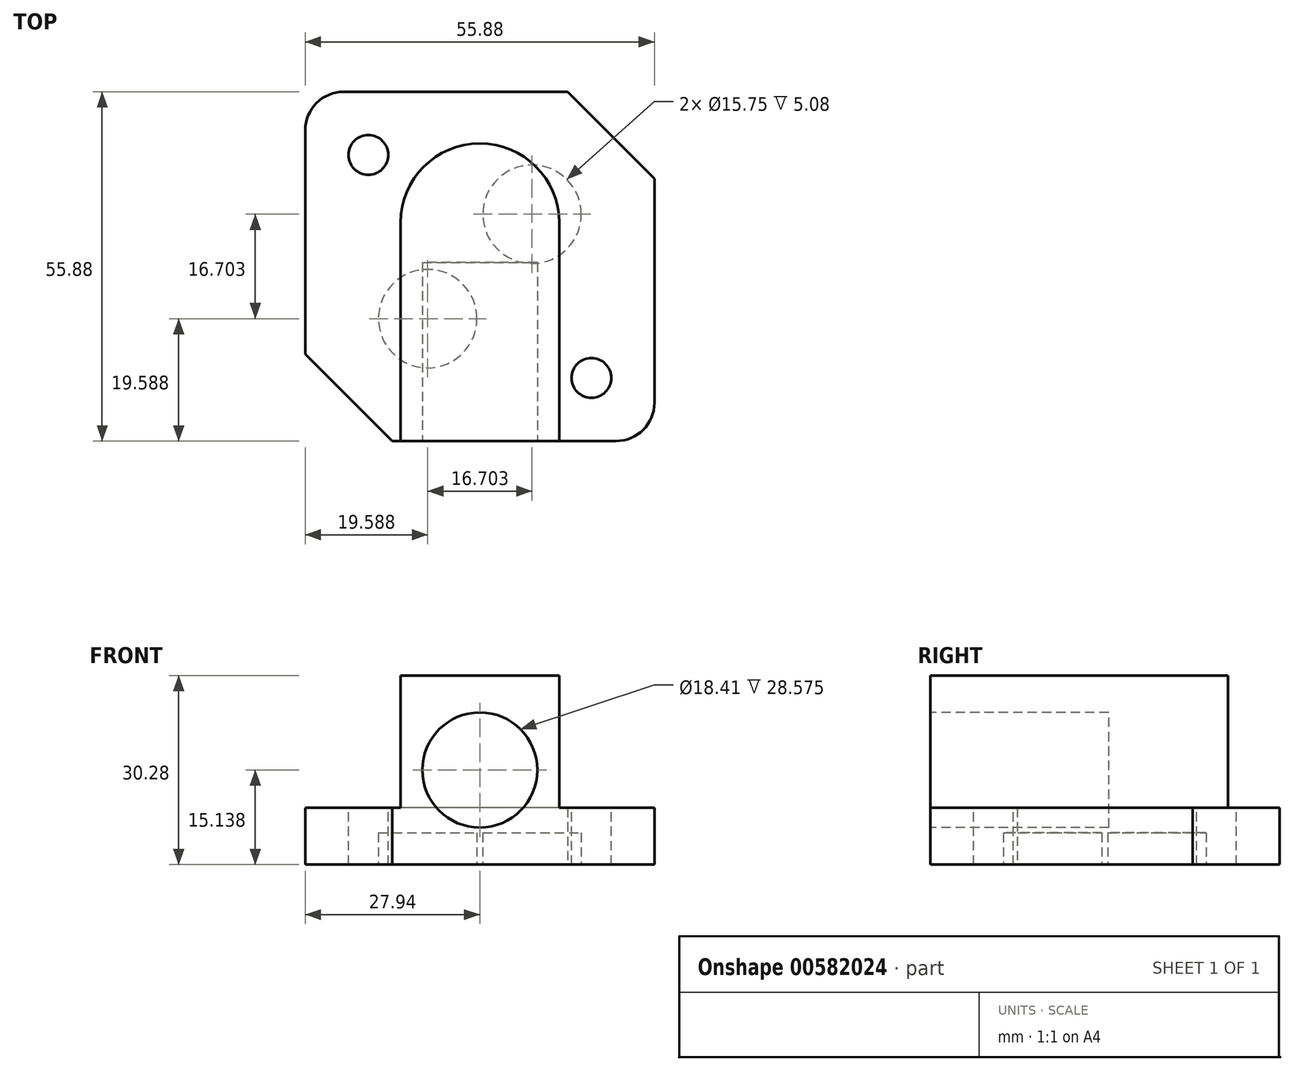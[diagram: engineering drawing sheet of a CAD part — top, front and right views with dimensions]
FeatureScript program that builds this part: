
annotation { "Feature Type Name" : "Feature", "Feature Type Description" : "" }
export const myFeature = defineFeature(function(context is Context, id is Id, definition is map)
    precondition{}
    {
        {
            var Q0;
            Q0=qCreatedBy(makeId("Top.planeOp"),FACE);
            var sketch = newSketch(context, id + "F0", { "sketchPlane" : qUnion([Q0])});
            skLineSegment(sketch, "E0.bottom", {"start": v(27.94, -27.94) * mm, "end": v(-27.94, -27.94) * mm, "construction": true});
            skLineSegment(sketch, "E0.top", {"start": v(27.94, 27.94) * mm, "end": v(-27.94, 27.94) * mm, "construction": true});
            skLineSegment(sketch, "E0.left", {"start": v(27.94, -27.94) * mm, "end": v(27.94, 27.94) * mm, "construction": true});
            skLineSegment(sketch, "E0.right", {"start": v(-27.94, -27.94) * mm, "end": v(-27.94, 27.94) * mm, "construction": true});
            skPoint(sketch, "E0.middle", {"position": v(0, 0) * mm});
            skLineSegment(sketch, "E1", {"start": v(-27.94, -14.03) * mm, "end": v(-14.03, -27.94) * mm});
            skLineSegment(sketch, "E2", {"start": v(14.03, 27.94) * mm, "end": v(27.94, 14.03) * mm});
            skLineSegment(sketch, "E3", {"start": v(-27.94, -27.94) * mm, "end": v(-20.99, -20.99) * mm, "construction": true});
            skLineSegment(sketch, "E4", {"start": v(-14.03, -27.94) * mm, "end": v(27.94, -27.94) * mm});
            skLineSegment(sketch, "E5", {"start": v(27.94, 14.03) * mm, "end": v(27.94, -27.94) * mm});
            skLineSegment(sketch, "E6", {"start": v(14.03, 27.94) * mm, "end": v(-27.94, 27.94) * mm});
            skLineSegment(sketch, "E7", {"start": v(-27.94, 27.94) * mm, "end": v(-27.94, -14.03) * mm});
            skSolve(sketch);
        }
        {
            var Q0;
            Q0 = qSketchRegion(id + "F0", true);
            extrude(context, id + "F1", {"entities" : qUnion([Q0]), "depth" : 9.1 * mm, "offsetDistance" : 25.4 * mm});
        }
        {
            var Q0;
            Q0=makeQuery(id+"F1.opExtrude","CAP_FACE",FACE,{"disambiguationData":[OSD([sQuery(id+"F0.wireOp",EDGE,"E1"),sQuery(id+"F0.wireOp",EDGE,"E2"),sQuery(id+"F0.wireOp",EDGE,"E4"),sQuery(id+"F0.wireOp",EDGE,"E5"),sQuery(id+"F0.wireOp",EDGE,"E6"),sQuery(id+"F0.wireOp",EDGE,"E7")])],"isStart":false});
            var sketch = newSketch(context, id + "F2", { "sketchPlane" : qUnion([Q0])});
            skArc(sketch, "E8", {"start": v(-12.7, 6.98) * mm, "mid": v(0, 19.68) * mm, "end": v(12.7, 6.98) * mm});
            skLineSegment(sketch, "E9", {"start": v(-12.7, 6.98) * mm, "end": v(-12.7, -27.94) * mm});
            skLineSegment(sketch, "E10", {"start": v(12.7, 6.98) * mm, "end": v(12.7, -27.94) * mm});
            skPoint(sketch, "E11", {"position": v(0, 19.68) * mm});
            skLineSegment(sketch, "E12", {"start": v(-12.7, -27.94) * mm, "end": v(12.7, -27.94) * mm});
            skSolve(sketch);
        }
        {
            var Q0;
            Q0 = qSketchRegion(id + "F2", true);
            extrude(context, id + "F3", {"entities" : qUnion([Q0]), "operationType" : NewBodyOperationType.ADD, "depth" : 21.18 * mm, "offsetDistance" : 25.4 * mm});
        }
        {
            var Q0;
            Q0=makeQuery(id+"F1.opExtrude","CAP_FACE",FACE,{"disambiguationData":[OSD([sQuery(id+"F0.wireOp",EDGE,"E1"),sQuery(id+"F0.wireOp",EDGE,"E2"),sQuery(id+"F0.wireOp",EDGE,"E4"),sQuery(id+"F0.wireOp",EDGE,"E5"),sQuery(id+"F0.wireOp",EDGE,"E6"),sQuery(id+"F0.wireOp",EDGE,"E7")])],"isStart":false});
            var sketch = newSketch(context, id + "F4", { "sketchPlane" : qUnion([Q0])});
            skArc(sketch, "E13", {"start": v(-27.94, 21.8) * mm, "mid": v(-26.14, 26.14) * mm, "end": v(-21.8, 27.94) * mm});
            skArc(sketch, "E14", {"start": v(21.8, -27.94) * mm, "mid": v(26.14, -26.14) * mm, "end": v(27.94, -21.8) * mm});
            skPoint(sketch, "E15", {"position": v(-26.14, 26.14) * mm});
            skPoint(sketch, "E16", {"position": v(26.14, -26.14) * mm});
            skLineSegment(sketch, "E17", {"start": v(-21.8, 21.8) * mm, "end": v(21.8, -21.8) * mm, "construction": true});
            skLineSegment(sketch, "E18", {"start": v(-27.94, 21.8) * mm, "end": v(-27.94, 27.94) * mm});
            skLineSegment(sketch, "E19", {"start": v(-27.94, 27.94) * mm, "end": v(-21.8, 27.94) * mm});
            skLineSegment(sketch, "E20", {"start": v(21.8, -27.94) * mm, "end": v(27.94, -27.94) * mm});
            skLineSegment(sketch, "E21", {"start": v(27.94, -27.94) * mm, "end": v(27.94, -21.8) * mm});
            skCircle(sketch, "E22", {"center": v(-17.84, 17.84) * mm, "radius": 3.18 * mm});
            skCircle(sketch, "E23", {"center": v(17.84, -17.84) * mm, "radius": 3.18 * mm});
            skPoint(sketch, "E24", {"position": v(-15.6, 15.6) * mm});
            skPoint(sketch, "E25", {"position": v(15.6, -15.6) * mm});
            skPoint(sketch, "E26", {"position": v(-20.09, 20.09) * mm});
            skPoint(sketch, "E27", {"position": v(20.09, -20.09) * mm});
            skLineSegment(sketch, "E28", {"start": v(-26.14, 26.14) * mm, "end": v(-17.84, 17.84) * mm, "construction": true});
            skLineSegment(sketch, "E29", {"start": v(26.14, -26.14) * mm, "end": v(17.84, -17.84) * mm, "construction": true});
            skSolve(sketch);
        }
        {
            var Q0;
            Q0 = qSketchRegion(id + "F4", true);
            extrude(context, id + "F5", {"entities" : qUnion([Q0]), "operationType" : NewBodyOperationType.REMOVE, "endBound" : BoundingType.THROUGH_ALL, "oppositeDirection" : true, "depth" : 25.4 * mm, "offsetDistance" : 25.4 * mm});
        }
        {
            var Q0;
            Q0=makeQuery(id+"F3.boolean.opBoolean","MERGE",FACE,{"derivedFrom":[makeQuery(id+"F1.opExtrude","SWEPT_FACE",FACE,{"disambiguationData":[OSD([sQuery(id+"F0.wireOp",EDGE,"E4")])]}),makeQuery(id+"F3.opExtrude","SWEPT_FACE",FACE,{"disambiguationData":[OSD([sQuery(id+"F2.wireOp",EDGE,"E12")])]})]});
            var sketch = newSketch(context, id + "F6", { "sketchPlane" : qUnion([Q0])});
            skLineSegment(sketch, "E30", {"start": v(0, 30.28) * mm, "end": v(0, 0) * mm, "construction": true});
            skCircle(sketch, "E31", {"center": v(0, 15.14) * mm, "radius": 9.2 * mm});
            skSolve(sketch);
        }
        {
            var Q0;
            Q0 = qSketchRegion(id + "F6", true);
            extrude(context, id + "F7", {"entities" : qUnion([Q0]), "operationType" : NewBodyOperationType.REMOVE, "oppositeDirection" : true, "depth" : 28.57 * mm, "offsetDistance" : 25.4 * mm});
        }
        {
            var Q0;
            Q0=makeQuery(id+"F1.opExtrude","CAP_FACE",FACE,{"disambiguationData":[OSD([sQuery(id+"F0.wireOp",EDGE,"E1"),sQuery(id+"F0.wireOp",EDGE,"E2"),sQuery(id+"F0.wireOp",EDGE,"E4"),sQuery(id+"F0.wireOp",EDGE,"E5"),sQuery(id+"F0.wireOp",EDGE,"E6"),sQuery(id+"F0.wireOp",EDGE,"E7")])],"isStart":true});
            var sketch = newSketch(context, id + "F8", { "sketchPlane" : qUnion([Q0])});
            skLineSegment(sketch, "E32", {"start": v(20.99, -20.99) * mm, "end": v(8.35, -8.35) * mm, "construction": true});
            skLineSegment(sketch, "E33", {"start": v(8.35, -8.35) * mm, "end": v(-8.35, 8.35) * mm, "construction": true});
            skLineSegment(sketch, "E34", {"start": v(-8.35, 8.35) * mm, "end": v(-20.99, 20.99) * mm, "construction": true});
            skCircle(sketch, "E35", {"center": v(8.35, -8.35) * mm, "radius": 7.87 * mm});
            skCircle(sketch, "E36", {"center": v(-8.35, 8.35) * mm, "radius": 7.87 * mm});
            skPoint(sketch, "E37", {"position": v(2.78, -2.78) * mm});
            skPoint(sketch, "E38", {"position": v(-2.78, 2.78) * mm});
            skPoint(sketch, "E39", {"position": v(13.92, -13.92) * mm});
            skPoint(sketch, "E40", {"position": v(-13.92, 13.92) * mm});
            skSolve(sketch);
        }
        {
            var Q0;
            Q0 = qSketchRegion(id + "F8", true);
            extrude(context, id + "F9", {"entities" : qUnion([Q0]), "operationType" : NewBodyOperationType.REMOVE, "oppositeDirection" : true, "depth" : 5.08 * mm, "offsetDistance" : 25.4 * mm});
        }
    });
